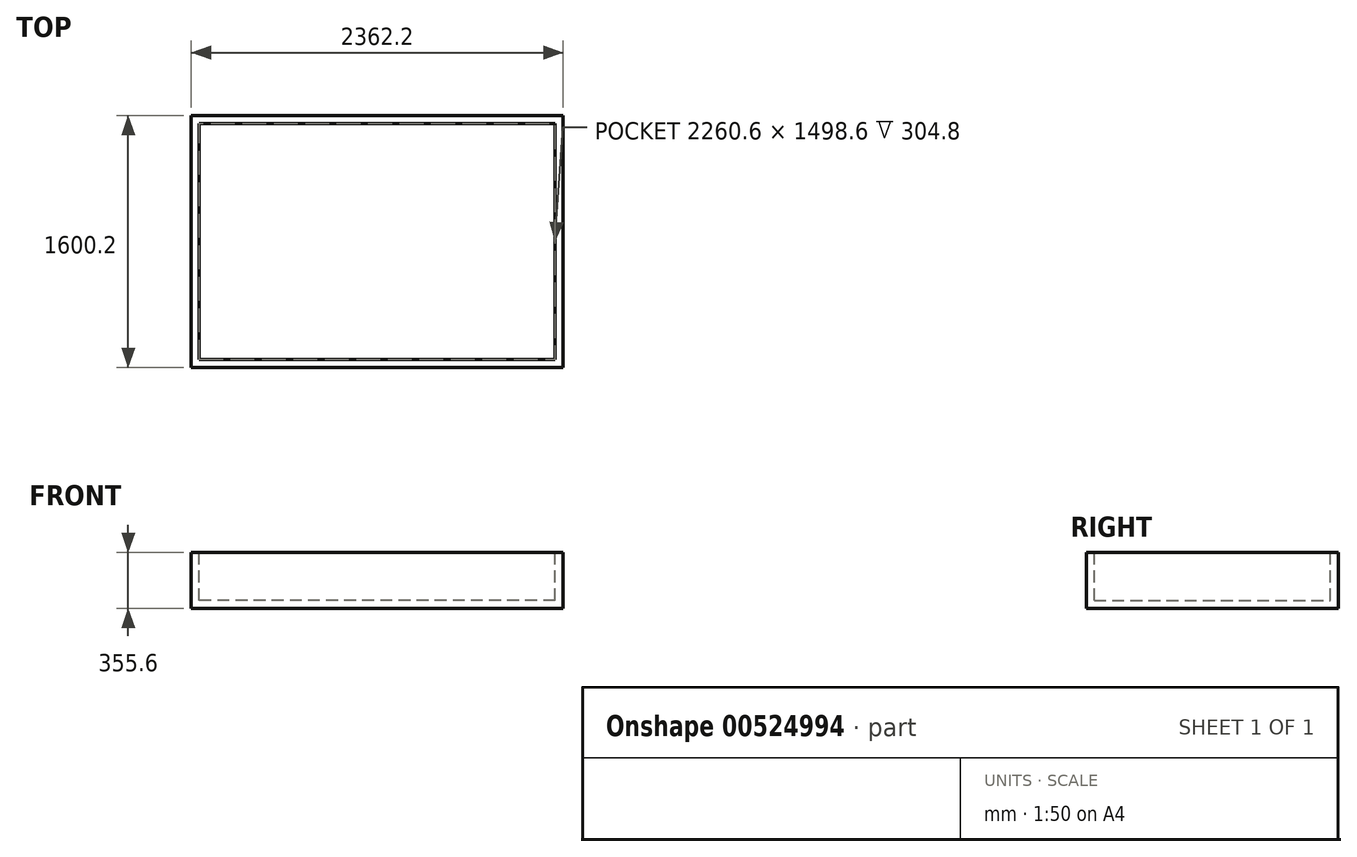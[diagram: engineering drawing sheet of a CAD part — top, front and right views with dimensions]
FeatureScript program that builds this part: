
annotation { "Feature Type Name" : "Feature", "Feature Type Description" : "" }
export const myFeature = defineFeature(function(context is Context, id is Id, definition is map)
    precondition{}
    {
        {
            var Q0;
            Q0=qCreatedBy(makeId("Front.planeOp"),FACE);
            var sketch = newSketch(context, id + "F0", { "sketchPlane" : qUnion([Q0])});
            skLineSegment(sketch, "E0.bottom", {"start": v(1181.1, -177.8) * mm, "end": v(-1181.1, -177.8) * mm});
            skLineSegment(sketch, "E0.top", {"start": v(1181.1, 177.8) * mm, "end": v(-1181.1, 177.8) * mm});
            skLineSegment(sketch, "E0.left", {"start": v(1181.1, -177.8) * mm, "end": v(1181.1, 177.8) * mm});
            skLineSegment(sketch, "E0.right", {"start": v(-1181.1, -177.8) * mm, "end": v(-1181.1, 177.8) * mm});
            skPoint(sketch, "E0.middle", {"position": v(0, 0) * mm});
            skSolve(sketch);
        }
        {
            var Q0;
            Q0=makeQuery(id+"F0.imprint","IMPRINT",FACE,{"disambiguationData":[TD([[makeQuery(id+"F0.imprint","IMPRINT",EDGE,{"derivedFrom":sQuery(id+"F0.wireOp",EDGE,"E0.bottom")}),-1.0]])]});
            extrude(context, id + "F1", {"entities" : qUnion([Q0]), "depth" : 1600.2 * mm, "offsetDistance" : 25.4 * mm});
        }
        {
            var Q0;
            Q0=makeQuery(id+"F1.opExtrude","SWEPT_FACE",FACE,{"disambiguationData":[OSD([sQuery(id+"F0.wireOp",EDGE,"E0.top")])]});
            shell(context, id + "F2", {"entities" : qUnion([Q0]), "thickness" : 50.8 * mm});
        }
    });
